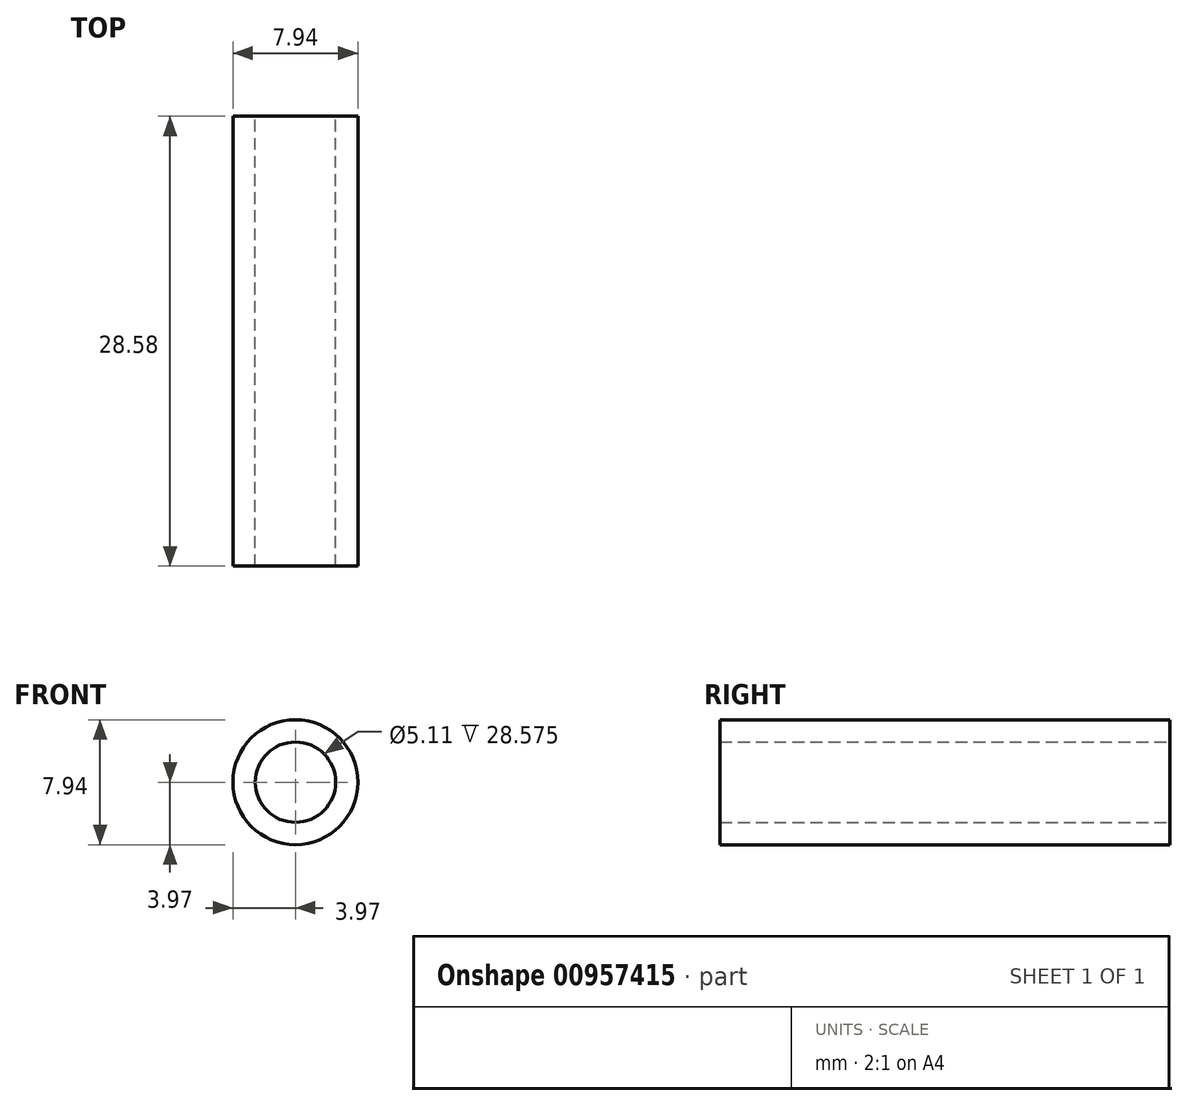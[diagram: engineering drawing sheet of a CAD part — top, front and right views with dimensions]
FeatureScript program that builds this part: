
annotation { "Feature Type Name" : "Feature", "Feature Type Description" : "" }
export const myFeature = defineFeature(function(context is Context, id is Id, definition is map)
    precondition{}
    {
        {
            var Q0;
            Q0=qCreatedBy(makeId("Front.planeOp"),FACE);
            var sketch = newSketch(context, id + "F0", { "sketchPlane" : qUnion([Q0])});
            skCircle(sketch, "E0", {"center": v(0, 0) * mm, "radius": 3.97 * mm});
            skCircle(sketch, "E1", {"center": v(0, 0) * mm, "radius": 2.55 * mm});
            skSolve(sketch);
        }
        {
            var Q0;
            Q0 = qSketchRegion(id + "F0", true);
            extrude(context, id + "F1", {"entities" : qUnion([Q0]), "depth" : 28.57 * mm, "offsetDistance" : 25.4 * mm});
        }
    });
